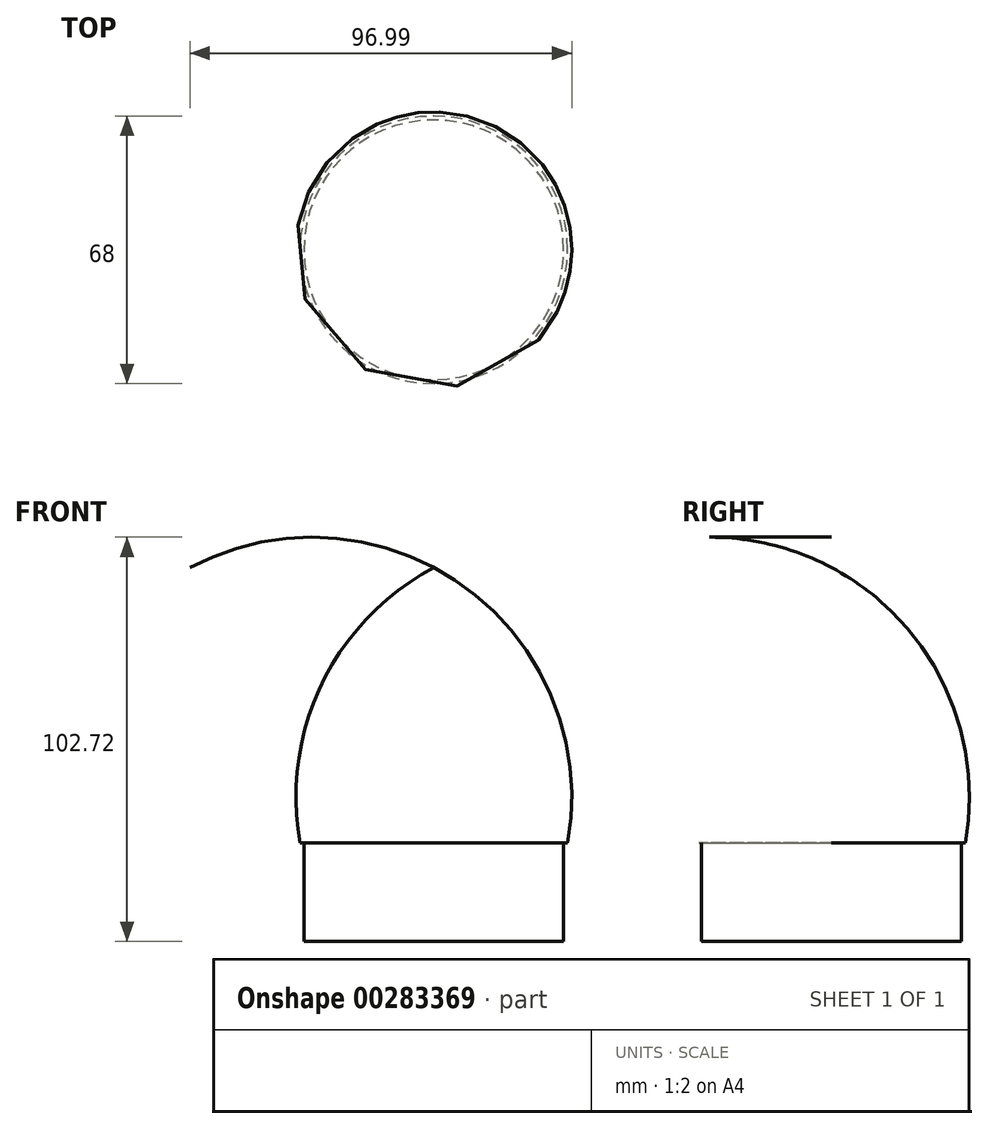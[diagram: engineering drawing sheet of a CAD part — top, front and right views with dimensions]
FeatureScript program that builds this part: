
annotation { "Feature Type Name" : "Feature", "Feature Type Description" : "" }
export const myFeature = defineFeature(function(context is Context, id is Id, definition is map)
    precondition{}
    {
        {
            var Q0;
            Q0=qCreatedBy(makeId("Front.planeOp"),FACE);
            var sketch = newSketch(context, id + "F0", { "sketchPlane" : qUnion([Q0])});
            skLineSegment(sketch, "E0", {"start": v(0, 27.64) * mm, "end": v(34, 27.64) * mm});
            skLineSegment(sketch, "E1", {"start": v(0, 27.64) * mm, "end": v(0, 97.64) * mm});
            skLineSegment(sketch, "E2", {"start": v(0, 20.97) * mm, "end": v(0, 112.46) * mm});
            skArc(sketch, "E3", {"start": v(34, 27.64) * mm, "mid": v(28.41, 68.18) * mm, "end": v(0, 97.64) * mm});
            skSolve(sketch);
        }
        {
            var Q0;
            {var subQ0=sQuery(id+"F0.wireOp",EDGE,"E0");Q0=makeQuery(id+"F0.imprint","IMPRINT",FACE,{"disambiguationData":[TD([[makeQuery(id+"F0.imprint","IMPRINT",EDGE,{"derivedFrom":subQ0}),1.0]])]});}
            var Q1;
            Q1=sQuery(id+"F0.wireOp",EDGE,"E2");
            revolve(context, id + "F1", {"entities" : qUnion([Q0]), "axis" : qUnion([Q1]), "revolveType" : RevolveType.FULL});
        }
        {
            var Q0;
            Q0=makeQuery(id+"F1.opRevolve","SWEPT_FACE",FACE,{"disambiguationData":[OSD([sQuery(id+"F0.wireOp",EDGE,"E0")])]});
            var sketch = newSketch(context, id + "F2", { "sketchPlane" : qUnion([Q0])});
            skCircle(sketch, "E4", {"center": v(0, 0) * mm, "radius": 33 * mm});
            skSolve(sketch);
        }
        {
            var Q0;
            Q0=makeQuery(id+"F2.imprint","IMPRINT",FACE,{"disambiguationData":[TD([[makeQuery(id+"F2.imprint","IMPRINT",EDGE,{"derivedFrom":sQuery(id+"F2.wireOp",EDGE,"E4")}),1.0]])]});
            extrude(context, id + "F3", {"entities" : qUnion([Q0]), "operationType" : NewBodyOperationType.ADD, "depth" : 25 * mm});
        }
    });
